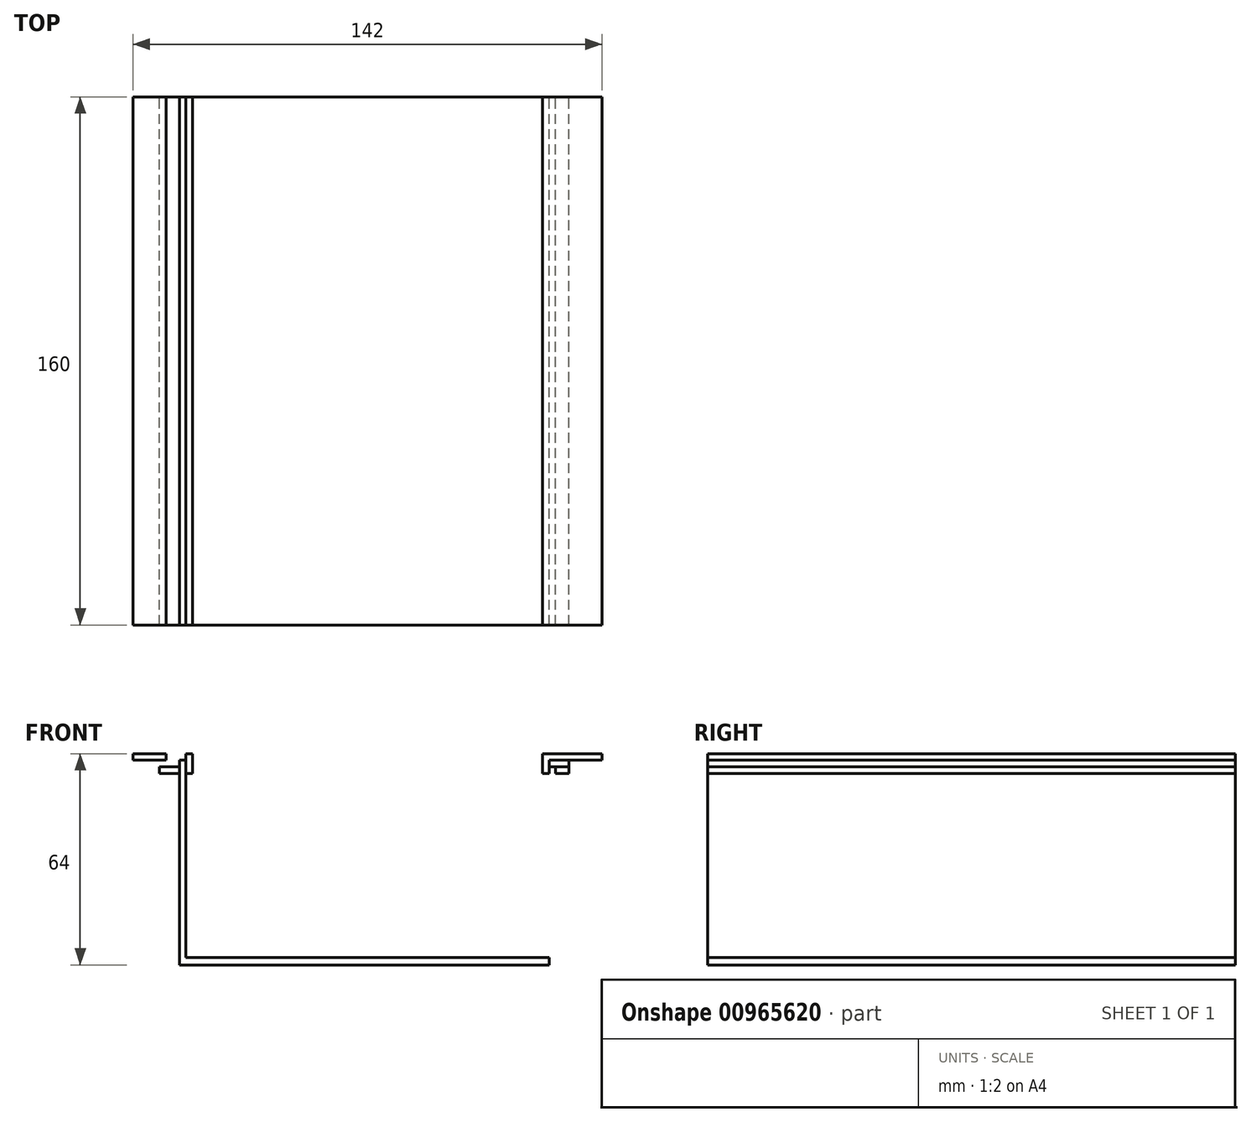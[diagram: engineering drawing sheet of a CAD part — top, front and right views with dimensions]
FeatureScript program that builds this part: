
annotation { "Feature Type Name" : "Feature", "Feature Type Description" : "" }
export const myFeature = defineFeature(function(context is Context, id is Id, definition is map)
    precondition{}
    {
        {
            var Q0;
            Q0=qCreatedBy(makeId("Front.planeOp"),FACE);
            var sketch = newSketch(context, id + "F0", { "sketchPlane" : qUnion([Q0])});
            skLineSegment(sketch, "E0.bottom", {"start": v(55, 30.99) * mm, "end": v(71, 30.99) * mm});
            skLineSegment(sketch, "E0.top", {"start": v(55, 32.99) * mm, "end": v(71, 32.99) * mm});
            skLineSegment(sketch, "E0.left", {"start": v(55, 30.99) * mm, "end": v(55, 32.99) * mm});
            skLineSegment(sketch, "E0.right", {"start": v(71, 30.99) * mm, "end": v(71, 32.99) * mm});
            skLineSegment(sketch, "E1.bottom", {"start": v(63, 30.99) * mm, "end": v(61, 30.99) * mm});
            skLineSegment(sketch, "E1.top", {"start": v(63, 26.99) * mm, "end": v(61, 26.99) * mm});
            skLineSegment(sketch, "E1.left", {"start": v(63, 30.99) * mm, "end": v(63, 26.99) * mm});
            skLineSegment(sketch, "E1.right", {"start": v(61, 30.99) * mm, "end": v(61, 26.99) * mm});
            skLineSegment(sketch, "E2.bottom", {"start": v(61, 26.99) * mm, "end": v(57, 26.99) * mm});
            skLineSegment(sketch, "E2.top", {"start": v(61, 28.99) * mm, "end": v(57, 28.99) * mm});
            skLineSegment(sketch, "E2.left", {"start": v(61, 26.99) * mm, "end": v(61, 28.99) * mm});
            skLineSegment(sketch, "E2.right", {"start": v(57, 26.99) * mm, "end": v(57, 28.99) * mm});
            skLineSegment(sketch, "E3.bottom", {"start": v(55, 32.99) * mm, "end": v(53, 32.99) * mm});
            skLineSegment(sketch, "E3.top", {"start": v(55, 26.99) * mm, "end": v(53, 26.99) * mm});
            skLineSegment(sketch, "E3.left", {"start": v(55, 32.99) * mm, "end": v(55, 26.99) * mm});
            skLineSegment(sketch, "E3.right", {"start": v(53, 32.99) * mm, "end": v(53, 26.99) * mm});
            skLineSegment(sketch, "E4.bottom", {"start": v(61, 28.99) * mm, "end": v(55, 28.99) * mm});
            skLineSegment(sketch, "E4.top", {"start": v(61, 30.99) * mm, "end": v(55, 30.99) * mm});
            skLineSegment(sketch, "E4.left", {"start": v(61, 28.99) * mm, "end": v(61, 30.99) * mm});
            skLineSegment(sketch, "E4.right", {"start": v(55, 28.99) * mm, "end": v(55, 30.99) * mm});
            skLineSegment(sketch, "E5.bottom", {"start": v(55, 28.99) * mm, "end": v(57, 28.99) * mm});
            skLineSegment(sketch, "E5.top", {"start": v(55, -31.01) * mm, "end": v(57, -31.01) * mm});
            skLineSegment(sketch, "E5.left", {"start": v(55, 28.99) * mm, "end": v(55, -31.01) * mm});
            skLineSegment(sketch, "E5.right", {"start": v(57, 28.99) * mm, "end": v(57, -31.01) * mm});
            skLineSegment(sketch, "E6.bottom", {"start": v(55, -31.01) * mm, "end": v(-55, -31.01) * mm});
            skLineSegment(sketch, "E6.top", {"start": v(55, -28.74) * mm, "end": v(-55, -28.74) * mm});
            skLineSegment(sketch, "E6.left", {"start": v(55, -31.01) * mm, "end": v(55, -28.74) * mm});
            skLineSegment(sketch, "E6.right", {"start": v(-55, -31.01) * mm, "end": v(-55, -28.74) * mm});
            skLineSegment(sketch, "E7.bottom", {"start": v(-55, -31.01) * mm, "end": v(-57, -31.01) * mm});
            skLineSegment(sketch, "E7.top", {"start": v(-55, 28.99) * mm, "end": v(-57, 28.99) * mm});
            skLineSegment(sketch, "E7.left", {"start": v(-55, -31.01) * mm, "end": v(-55, 28.99) * mm});
            skLineSegment(sketch, "E7.right", {"start": v(-57, -31.01) * mm, "end": v(-57, 28.99) * mm});
            skLineSegment(sketch, "E8.top", {"start": v(-55, 30.99) * mm, "end": v(-57, 30.99) * mm});
            skLineSegment(sketch, "E8.left", {"start": v(-55, 28.99) * mm, "end": v(-55, 30.99) * mm});
            skLineSegment(sketch, "E8.right", {"start": v(-57, 28.99) * mm, "end": v(-57, 30.99) * mm});
            skLineSegment(sketch, "E9.bottom", {"start": v(-57, 30.99) * mm, "end": v(-61, 30.99) * mm});
            skLineSegment(sketch, "E9.top", {"start": v(-57, 28.99) * mm, "end": v(-61, 28.99) * mm});
            skLineSegment(sketch, "E9.left", {"start": v(-57, 30.99) * mm, "end": v(-57, 28.99) * mm});
            skLineSegment(sketch, "E9.right", {"start": v(-61, 30.99) * mm, "end": v(-61, 28.99) * mm});
            skLineSegment(sketch, "E10.bottom", {"start": v(-57, 28.99) * mm, "end": v(-63, 28.99) * mm});
            skLineSegment(sketch, "E10.top", {"start": v(-57, 26.99) * mm, "end": v(-63, 26.99) * mm});
            skLineSegment(sketch, "E10.left", {"start": v(-57, 28.99) * mm, "end": v(-57, 26.99) * mm});
            skLineSegment(sketch, "E10.right", {"start": v(-63, 28.99) * mm, "end": v(-63, 26.99) * mm});
            skLineSegment(sketch, "E11.bottom", {"start": v(-63, 28.99) * mm, "end": v(-61, 28.99) * mm});
            skLineSegment(sketch, "E11.top", {"start": v(-63, 32.99) * mm, "end": v(-61, 32.99) * mm});
            skLineSegment(sketch, "E11.left", {"start": v(-63, 28.99) * mm, "end": v(-63, 32.99) * mm});
            skLineSegment(sketch, "E11.right", {"start": v(-61, 28.99) * mm, "end": v(-61, 32.99) * mm});
            skLineSegment(sketch, "E12.bottom", {"start": v(-55, 26.99) * mm, "end": v(-53, 26.99) * mm});
            skLineSegment(sketch, "E12.top", {"start": v(-55, 32.99) * mm, "end": v(-53, 32.99) * mm});
            skLineSegment(sketch, "E12.left", {"start": v(-55, 26.99) * mm, "end": v(-55, 32.99) * mm});
            skLineSegment(sketch, "E12.right", {"start": v(-53, 26.99) * mm, "end": v(-53, 32.99) * mm});
            skLineSegment(sketch, "E13.bottom", {"start": v(-55, 32.99) * mm, "end": v(-71, 32.99) * mm});
            skLineSegment(sketch, "E13.top", {"start": v(-55, 30.99) * mm, "end": v(-71, 30.99) * mm});
            skLineSegment(sketch, "E13.left", {"start": v(-55, 32.99) * mm, "end": v(-55, 30.99) * mm});
            skLineSegment(sketch, "E13.right", {"start": v(-71, 32.99) * mm, "end": v(-71, 30.99) * mm});
            skSolve(sketch);
        }
        {
            var Q0;
            Q0=makeQuery(id+"F0.imprint","IMPRINT",FACE,{"disambiguationData":[TD([[makeQuery(id+"F0.imprint","IMPRINT",EDGE,{"derivedFrom":sQuery(id+"F0.wireOp",EDGE,"E0.top")}),-1.0]])]});
            var Q1;
            Q1=makeQuery(id+"F0.imprint","IMPRINT",FACE,{"disambiguationData":[TD([[makeQuery(id+"F0.imprint","IMPRINT",EDGE,{"derivedFrom":sQuery(id+"F0.wireOp",EDGE,"E1.bottom")}),1.0]])]});
            var Q2;
            Q2=makeQuery(id+"F0.imprint","IMPRINT",FACE,{"disambiguationData":[TD([[makeQuery(id+"F0.imprint","IMPRINT",EDGE,{"derivedFrom":sQuery(id+"F0.wireOp",EDGE,"E2.bottom")}),-1.0]])]});
            var Q3;
            {var subQ3=sQuery(id+"F0.wireOp",EDGE,"E3.bottom");Q3=makeQuery(id+"F0.imprint","IMPRINT",FACE,{"disambiguationData":[TD([[makeQuery(id+"F0.imprint","IMPRINT",EDGE,{"derivedFrom":subQ3}),1.0]])]});}
            var Q4;
            {var subQ3=sQuery(id+"F0.wireOp",EDGE,"E12.bottom");Q4=makeQuery(id+"F0.imprint","IMPRINT",FACE,{"disambiguationData":[TD([[makeQuery(id+"F0.imprint","IMPRINT",EDGE,{"derivedFrom":subQ3}),1.0]])]});}
            var Q5;
            {var subQ2=sQuery(id+"F0.wireOp",EDGE,"E13.left");Q5=makeQuery(id+"F0.imprint","IMPRINT",FACE,{"disambiguationData":[TD([[makeQuery(id+"F0.imprint","IMPRINT",EDGE,{"derivedFrom":subQ2}),-1.0]])]});}
            var Q6;
            {var subQ0=sQuery(id+"F0.wireOp",EDGE,"E13.bottom");var subQ1=sQuery(id+"F0.wireOp",EDGE,"E11.left");var subQ2=makeQuery(id+"F0.imprint","INTERSECT",VERTEX,{"derivedFrom":[subQ1,subQ0]});Q6=makeQuery(id+"F0.imprint","IMPRINT",FACE,{"disambiguationData":[TD([[makeQuery(id+"F0.imprint","IMPRINT",EDGE,{"disambiguationData":[TD([[subQ2,1.0]])],"derivedFrom":subQ1}),-1.0]])]});}
            var Q7;
            {var subQ0=sQuery(id+"F0.wireOp",EDGE,"E11.bottom");Q7=makeQuery(id+"F0.imprint","IMPRINT",FACE,{"disambiguationData":[TD([[makeQuery(id+"F0.imprint","IMPRINT",EDGE,{"derivedFrom":subQ0}),1.0]])]});}
            var Q8;
            Q8=makeQuery(id+"F0.imprint","IMPRINT",FACE,{"disambiguationData":[TD([[makeQuery(id+"F0.imprint","IMPRINT",EDGE,{"derivedFrom":sQuery(id+"F0.wireOp",EDGE,"E10.bottom")}),1.0]])]});
            var Q9;
            {var subQ5=sQuery(id+"F0.wireOp",EDGE,"E13.right");Q9=makeQuery(id+"F0.imprint","IMPRINT",FACE,{"disambiguationData":[TD([[makeQuery(id+"F0.imprint","IMPRINT",EDGE,{"derivedFrom":subQ5}),1.0]])]});}
            extrude(context, id + "F1", {"entities" : qUnion([Q0, Q1, Q2, Q3, Q4, Q5, Q6, Q7, Q8, Q9]), "depth" : 80 * mm, "offsetDistance" : 25 * mm, "hasSecondDirection" : true, "secondDirectionOppositeDirection" : true, "secondDirectionDepth" : 80 * mm});
        }
        {
            var Q0;
            Q0=makeQuery(id+"F0.imprint","IMPRINT",FACE,{"disambiguationData":[TD([[makeQuery(id+"F0.imprint","IMPRINT",EDGE,{"derivedFrom":sQuery(id+"F0.wireOp",EDGE,"E4.bottom")}),-1.0]])]});
            var Q1;
            {var subQ3=sQuery(id+"F0.wireOp",EDGE,"E5.bottom");Q1=makeQuery(id+"F0.imprint","IMPRINT",FACE,{"disambiguationData":[TD([[makeQuery(id+"F0.imprint","IMPRINT",EDGE,{"derivedFrom":subQ3}),-1.0]])]});}
            var Q2;
            {var subQ0=sQuery(id+"F0.wireOp",EDGE,"E6.bottom");Q2=makeQuery(id+"F0.imprint","IMPRINT",FACE,{"disambiguationData":[TD([[makeQuery(id+"F0.imprint","IMPRINT",EDGE,{"derivedFrom":subQ0}),-1.0]])]});}
            var Q3;
            {var subQ4=sQuery(id+"F0.wireOp",EDGE,"E7.bottom");Q3=makeQuery(id+"F0.imprint","IMPRINT",FACE,{"disambiguationData":[TD([[makeQuery(id+"F0.imprint","IMPRINT",EDGE,{"derivedFrom":subQ4}),-1.0]])]});}
            var Q4;
            {var subQ0=sQuery(id+"F0.wireOp",EDGE,"E9.left");Q4=makeQuery(id+"F0.imprint","IMPRINT",FACE,{"disambiguationData":[TD([[makeQuery(id+"F0.imprint","IMPRINT",EDGE,{"derivedFrom":subQ0}),-1.0]])]});}
            var Q5;
            {var subQ0=sQuery(id+"F0.wireOp",EDGE,"E7.top");Q5=makeQuery(id+"F0.imprint","IMPRINT",FACE,{"disambiguationData":[TD([[makeQuery(id+"F0.imprint","IMPRINT",EDGE,{"derivedFrom":subQ0}),-1.0]])]});}
            extrude(context, id + "F2", {"entities" : qUnion([Q0, Q1, Q2, Q3, Q4, Q5]), "depth" : 80 * mm, "offsetDistance" : 25 * mm, "hasSecondDirection" : true, "secondDirectionOppositeDirection" : true, "secondDirectionDepth" : 80 * mm});
        }
    });
